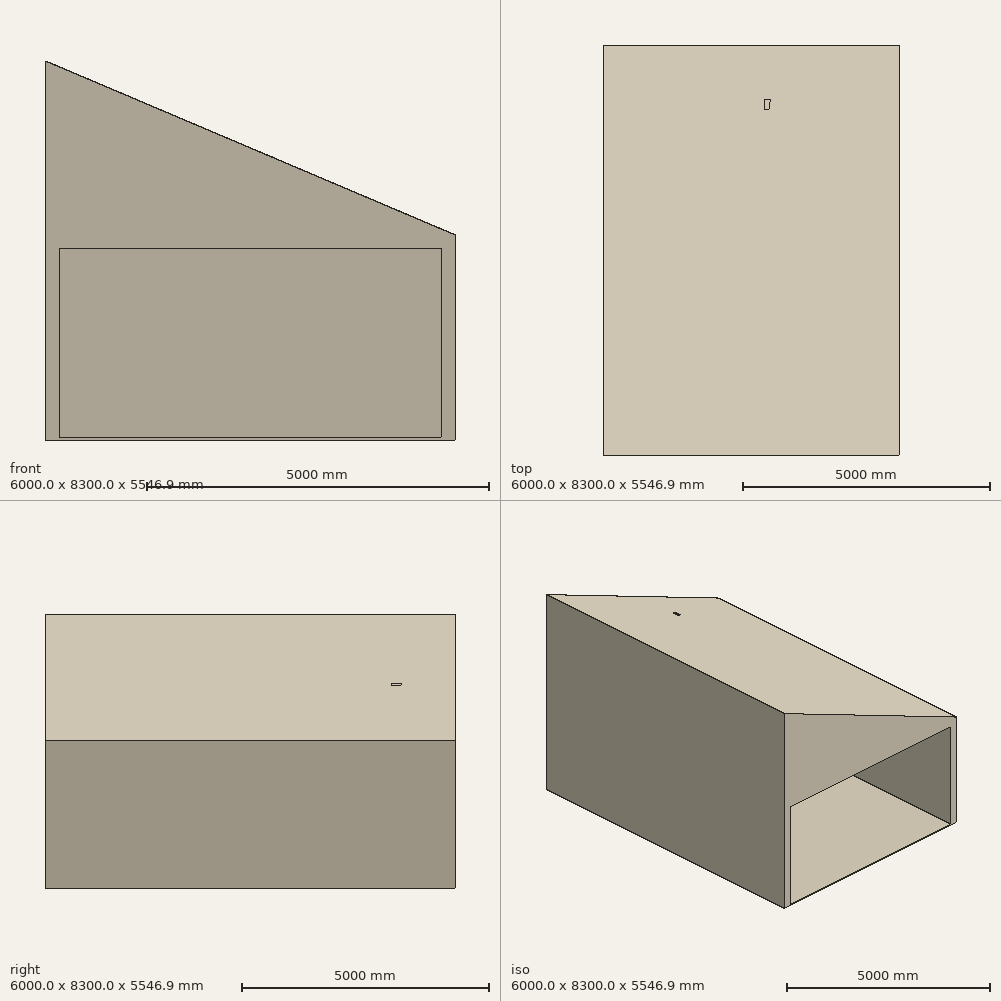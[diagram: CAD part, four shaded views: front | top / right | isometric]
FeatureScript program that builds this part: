
annotation { "Feature Type Name" : "Feature", "Feature Type Description" : "" }
export const myFeature = defineFeature(function(context is Context, id is Id, definition is map)
    precondition{}
    {
        {
            var Q0;
            Q0=qCreatedBy(makeId("Top.planeOp"),FACE);
            var sketch = newSketch(context, id + "F0", { "sketchPlane" : qUnion([Q0])});
            skLineSegment(sketch, "E0.bottom", {"start": v(0, 8300) * mm, "end": v(6000, 8300) * mm});
            skLineSegment(sketch, "E0.top", {"start": v(0, 0) * mm, "end": v(6000, 0) * mm});
            skLineSegment(sketch, "E0.left", {"start": v(0, 8300) * mm, "end": v(0, 0) * mm});
            skLineSegment(sketch, "E0.right", {"start": v(6000, 8300) * mm, "end": v(6000, 0) * mm});
            skSolve(sketch);
        }
        {
            var Q0;
            Q0 = qSketchRegion(id + "F0", true);
            extrude(context, id + "F1", {"entities" : qUnion([Q0]), "depth" : 3000 * mm, "offsetDistance" : 25 * mm});
        }
        {
            var Q0;
            Q0=makeQuery(id+"F1.opExtrude","SWEPT_FACE",FACE,{"disambiguationData":[OSD([sQuery(id+"F0.wireOp",EDGE,"E0.top")])]});
            var sketch = newSketch(context, id + "F2", { "sketchPlane" : qUnion([Q0])});
            skLineSegment(sketch, "E1.bottom", {"start": v(200, 2800) * mm, "end": v(5800, 2800) * mm});
            skLineSegment(sketch, "E1.left", {"start": v(200, 2800) * mm, "end": v(200, 30) * mm});
            skLineSegment(sketch, "E1.right", {"start": v(5800, 2800) * mm, "end": v(5800, 30) * mm});
            skLineSegment(sketch, "E2", {"start": v(200, 30) * mm, "end": v(5800, 30) * mm});
            skSolve(sketch);
        }
        {
            var Q0;
            Q0 = qSketchRegion(id + "F2", true);
            extrude(context, id + "F3", {"entities" : qUnion([Q0]), "operationType" : NewBodyOperationType.REMOVE, "oppositeDirection" : true, "depth" : 8200 * mm, "offsetDistance" : 25 * mm});
        }
        {
            var Q0;
            Q0=makeQuery(id+"F1.opExtrude","CAP_FACE",FACE,{"disambiguationData":[OSD([sQuery(id+"F0.wireOp",EDGE,"E0.bottom"),sQuery(id+"F0.wireOp",EDGE,"E0.top"),sQuery(id+"F0.wireOp",EDGE,"E0.left"),sQuery(id+"F0.wireOp",EDGE,"E0.right")])],"isStart":false});
            var sketch = newSketch(context, id + "F4", { "sketchPlane" : qUnion([Q0])});
            skLineSegment(sketch, "E3", {"start": v(3000, 0) * mm, "end": v(3000, 8000) * mm});
            skPoint(sketch, "E3.endSnap0", {"position": v(3000, 8300) * mm});
            skLineSegment(sketch, "E4", {"start": v(3000, 8000) * mm, "end": v(200, 8000) * mm});
            skLineSegment(sketch, "E5", {"start": v(200, 8000) * mm, "end": v(200, 0) * mm});
            skLineSegment(sketch, "E6", {"start": v(200, 0) * mm, "end": v(3000, 0) * mm});
            skSolve(sketch);
        }
        {
            var Q0;
            Q0 = qSketchRegion(id + "F4", true);
            extrude(context, id + "F5", {"entities" : qUnion([Q0]), "operationType" : NewBodyOperationType.REMOVE, "oppositeDirection" : true, "depth" : 200 * mm, "offsetDistance" : 25 * mm});
        }
        {
            var Q0;
            Q0=makeQuery(id+"F1.opExtrude","SWEPT_FACE",FACE,{"disambiguationData":[OSD([sQuery(id+"F0.wireOp",EDGE,"E0.top")])]});
            var sketch = newSketch(context, id + "F6", { "sketchPlane" : qUnion([Q0])});
            skLineSegment(sketch, "E7", {"start": v(0, 5546.85) * mm, "end": v(0, 3000) * mm});
            skLineSegment(sketch, "E8", {"start": v(0, 3000) * mm, "end": v(6000, 3000) * mm});
            skLineSegment(sketch, "E9", {"start": v(0, 5546.85) * mm, "end": v(6000, 3000) * mm});
            skSolve(sketch);
        }
        {
            var Q0;
            Q0 = qSketchRegion(id + "F6", true);
            extrude(context, id + "F7", {"entities" : qUnion([Q0]), "operationType" : NewBodyOperationType.ADD, "oppositeDirection" : true, "depth" : 8300 * mm, "offsetDistance" : 25 * mm});
        }
        {
            var Q0;
            Q0=makeQuery(id+"F7.boolean.opBoolean","MERGE",FACE,{"derivedFrom":[makeQuery(id+"F1.opExtrude","SWEPT_FACE",FACE,{"disambiguationData":[OSD([sQuery(id+"F0.wireOp",EDGE,"E0.top")])]}),makeQuery(id+"F7.opExtrude","CAP_FACE",FACE,{"disambiguationData":[OSD([sQuery(id+"F6.wireOp",EDGE,"Ax6CvXE0-xQUs-nxLp-Lo4a-HNlgkfwtuCLE"),sQuery(id+"F6.wireOp",EDGE,"HgU5PMEn-LdUz-rNYr-L3yG-fbvhLAGtGccu"),sQuery(id+"F6.wireOp",EDGE,"E7"),sQuery(id+"F6.wireOp",EDGE,"E8")])],"isStart":true})]});
            var sketch = newSketch(context, id + "F8", { "sketchPlane" : qUnion([Q0])});
            skLineSegment(sketch, "E10", {"start": v(5800, 3000) * mm, "end": v(5800, 2900) * mm});
            skLineSegment(sketch, "E11", {"start": v(5800, 2900) * mm, "end": v(3000, 2900) * mm});
            skLineSegment(sketch, "E12", {"start": v(3000, 2900) * mm, "end": v(3000, 2800) * mm});
            skLineSegment(sketch, "E13", {"start": v(3000, 2800) * mm, "end": v(200, 2800) * mm});
            skLineSegment(sketch, "E14", {"start": v(200, 2800) * mm, "end": v(200, 5377.06) * mm});
            skLineSegment(sketch, "E15", {"start": v(200, 5377.06) * mm, "end": v(5800, 3000) * mm});
            skSolve(sketch);
        }
        {
            var Q0;
            Q0 = qSketchRegion(id + "F8", true);
            extrude(context, id + "F9", {"entities" : qUnion([Q0]), "operationType" : NewBodyOperationType.REMOVE, "oppositeDirection" : true, "depth" : 8200 * mm, "offsetDistance" : 25 * mm});
        }
        {
            var Q0;
            Q0=makeQuery(id+"F9.boolean.opBoolean","COPY",FACE,{"derivedFrom":makeQuery(id+"F9.opExtrude","SWEPT_FACE",FACE,{"disambiguationData":[OSD([sQuery(id+"F8.wireOp",EDGE,"E11")])]})});
            var sketch = newSketch(context, id + "F10", { "sketchPlane" : qUnion([Q0])});
            skLineSegment(sketch, "E16", {"start": v(3300, 1000) * mm, "end": v(3300, 1200) * mm});
            skLineSegment(sketch, "E17", {"start": v(3300, 1200) * mm, "end": v(3100, 1200) * mm});
            skLineSegment(sketch, "E18", {"start": v(3100, 1200) * mm, "end": v(3100, 1000) * mm});
            skLineSegment(sketch, "E19", {"start": v(3100, 1000) * mm, "end": v(3300, 1000) * mm});
            skLineSegment(sketch, "E20", {"start": v(3200, 0) * mm, "end": v(3300, 8200) * mm, "construction": true});
            skPoint(sketch, "E20.startSnap0", {"position": v(3200, 1000) * mm});
            skLineSegment(sketch, "E21", {"start": v(3250, 4100) * mm, "end": v(1614.91, 4119.94) * mm, "construction": true});
            skLineSegment(sketch, "E22.MirrorCS", {"start": v(3375.58, 7197.86) * mm, "end": v(3370.7, 6997.92) * mm});
            skLineSegment(sketch, "E23.MirrorCS", {"start": v(3175.64, 7202.74) * mm, "end": v(3375.58, 7197.86) * mm});
            skLineSegment(sketch, "E24.MirrorCS", {"start": v(3170.77, 7002.8) * mm, "end": v(3175.64, 7202.74) * mm});
            skLineSegment(sketch, "E25.MirrorCS", {"start": v(3370.7, 6997.92) * mm, "end": v(3170.77, 7002.8) * mm});
            skSolve(sketch);
        }
        {
            var Q0;
            Q0 = qSketchRegion(id + "F10", true);
            extrude(context, id + "F11", {"entities" : qUnion([Q0]), "operationType" : NewBodyOperationType.ADD, "depth" : 1260 * mm, "offsetDistance" : 25 * mm});
        }
        {
            var Q0;
            {var subQ1=sQuery(id+"F10.wireOp",EDGE,"E19");Q0=makeQuery(id+"F11.boolean.opBoolean","SPLIT",FACE,{"disambiguationData":[TD([makeQuery(id+"F7.opExtrude","SWEPT_FACE",FACE,{"disambiguationData":[OSD([sQuery(id+"F6.wireOp",EDGE,"E9")])]})])],"derivedFrom":makeQuery(id+"F11.opExtrude","SWEPT_FACE",FACE,{"disambiguationData":[OSD([subQ1])]})});}
            var sketch = newSketch(context, id + "F12", { "sketchPlane" : qUnion([Q0])});
            skLineSegment(sketch, "E26", {"start": v(3300, 4146.08) * mm, "end": v(3267.21, 4160) * mm});
            skLineSegment(sketch, "E27", {"start": v(3267.21, 4160) * mm, "end": v(3300, 4160) * mm});
            skLineSegment(sketch, "E28", {"start": v(3300, 4160) * mm, "end": v(3300, 4146.08) * mm});
            skSolve(sketch);
        }
        {
            var Q0;
            Q0 = qSketchRegion(id + "F12", true);
            extrude(context, id + "F13", {"entities" : qUnion([Q0]), "operationType" : NewBodyOperationType.REMOVE, "oppositeDirection" : true, "depth" : 262 * mm, "offsetDistance" : 25 * mm});
        }
        {
            var Q0;
            {var subQ1=sQuery(id+"F10.wireOp",EDGE,"E25.MirrorCS");Q0=makeQuery(id+"F11.boolean.opBoolean","SPLIT",FACE,{"disambiguationData":[TD([makeQuery(id+"F7.opExtrude","SWEPT_FACE",FACE,{"disambiguationData":[OSD([sQuery(id+"F6.wireOp",EDGE,"E9")])]})])],"derivedFrom":makeQuery(id+"F11.opExtrude","SWEPT_FACE",FACE,{"disambiguationData":[OSD([subQ1])]})});}
            var sketch = newSketch(context, id + "F14", { "sketchPlane" : qUnion([Q0])});
            skLineSegment(sketch, "E29", {"start": v(3095.52, 4160) * mm, "end": v(3199.05, 4116.07) * mm});
            skLineSegment(sketch, "E30", {"start": v(3199.05, 4116.07) * mm, "end": v(3199.05, 4160) * mm});
            skLineSegment(sketch, "E31", {"start": v(3199.05, 4160) * mm, "end": v(3095.52, 4160) * mm});
            skSolve(sketch);
        }
        {
            var Q0;
            Q0 = qSketchRegion(id + "F14", true);
            extrude(context, id + "F15", {"entities" : qUnion([Q0]), "operationType" : NewBodyOperationType.REMOVE, "oppositeDirection" : true, "depth" : 230.2 * mm, "offsetDistance" : 25 * mm});
        }
        {
            var Q0;
            Q0=makeQuery(id+"F7.boolean.opBoolean","MERGE",FACE,{"derivedFrom":[makeQuery(id+"F1.opExtrude","SWEPT_FACE",FACE,{"disambiguationData":[OSD([sQuery(id+"F0.wireOp",EDGE,"E0.top")])]}),makeQuery(id+"F7.opExtrude","CAP_FACE",FACE,{"disambiguationData":[OSD([sQuery(id+"F6.wireOp",EDGE,"E7"),sQuery(id+"F6.wireOp",EDGE,"E8"),sQuery(id+"F6.wireOp",EDGE,"E9")])],"isStart":true})]});
            var sketch = newSketch(context, id + "F16", { "sketchPlane" : qUnion([Q0])});
            skLineSegment(sketch, "E32", {"start": v(5800, 2900) * mm, "end": v(5800, 3000) * mm});
            skLineSegment(sketch, "E33", {"start": v(5800, 3000) * mm, "end": v(200, 5377.06) * mm});
            skLineSegment(sketch, "E34", {"start": v(200, 5377.06) * mm, "end": v(200, 2900) * mm});
            skLineSegment(sketch, "E35", {"start": v(200, 2900) * mm, "end": v(5800, 2900) * mm});
            skSolve(sketch);
        }
        {
            var Q0;
            Q0 = qSketchRegion(id + "F16", true);
            extrude(context, id + "F17", {"entities" : qUnion([Q0]), "operationType" : NewBodyOperationType.ADD, "oppositeDirection" : true, "depth" : 40 * mm, "offsetDistance" : 25 * mm});
        }
        {
            var Q0;
            Q0=makeQuery(id+"F17.boolean.opBoolean","MERGE",FACE,{"derivedFrom":[makeQuery(id+"F7.boolean.opBoolean","MERGE",FACE,{"derivedFrom":[makeQuery(id+"F1.opExtrude","SWEPT_FACE",FACE,{"disambiguationData":[OSD([sQuery(id+"F0.wireOp",EDGE,"E0.top")])]}),makeQuery(id+"F7.opExtrude","CAP_FACE",FACE,{"disambiguationData":[OSD([sQuery(id+"F6.wireOp",EDGE,"E7"),sQuery(id+"F6.wireOp",EDGE,"E8"),sQuery(id+"F6.wireOp",EDGE,"E9")])],"isStart":true})]}),makeQuery(id+"F17.opExtrude","CAP_FACE",FACE,{"disambiguationData":[OSD([sQuery(id+"F16.wireOp",EDGE,"E32"),sQuery(id+"F16.wireOp",EDGE,"E33"),sQuery(id+"F16.wireOp",EDGE,"E34"),sQuery(id+"F16.wireOp",EDGE,"E35")])],"isStart":true})]});
            var sketch = newSketch(context, id + "F18", { "sketchPlane" : qUnion([Q0])});
            skLineSegment(sketch, "E36", {"start": v(3000, 2800) * mm, "end": v(200, 2800) * mm});
            skLineSegment(sketch, "E37", {"start": v(200, 2800) * mm, "end": v(200, 2900) * mm});
            skLineSegment(sketch, "E38", {"start": v(200, 2900) * mm, "end": v(3000, 2900) * mm});
            skLineSegment(sketch, "E39", {"start": v(3000, 2900) * mm, "end": v(3000, 2800) * mm});
            skSolve(sketch);
        }
        {
            var Q0;
            Q0 = qSketchRegion(id + "F18", true);
            extrude(context, id + "F19", {"entities" : qUnion([Q0]), "operationType" : NewBodyOperationType.ADD, "oppositeDirection" : true, "depth" : 80 * mm, "offsetDistance" : 25 * mm});
        }
    });
